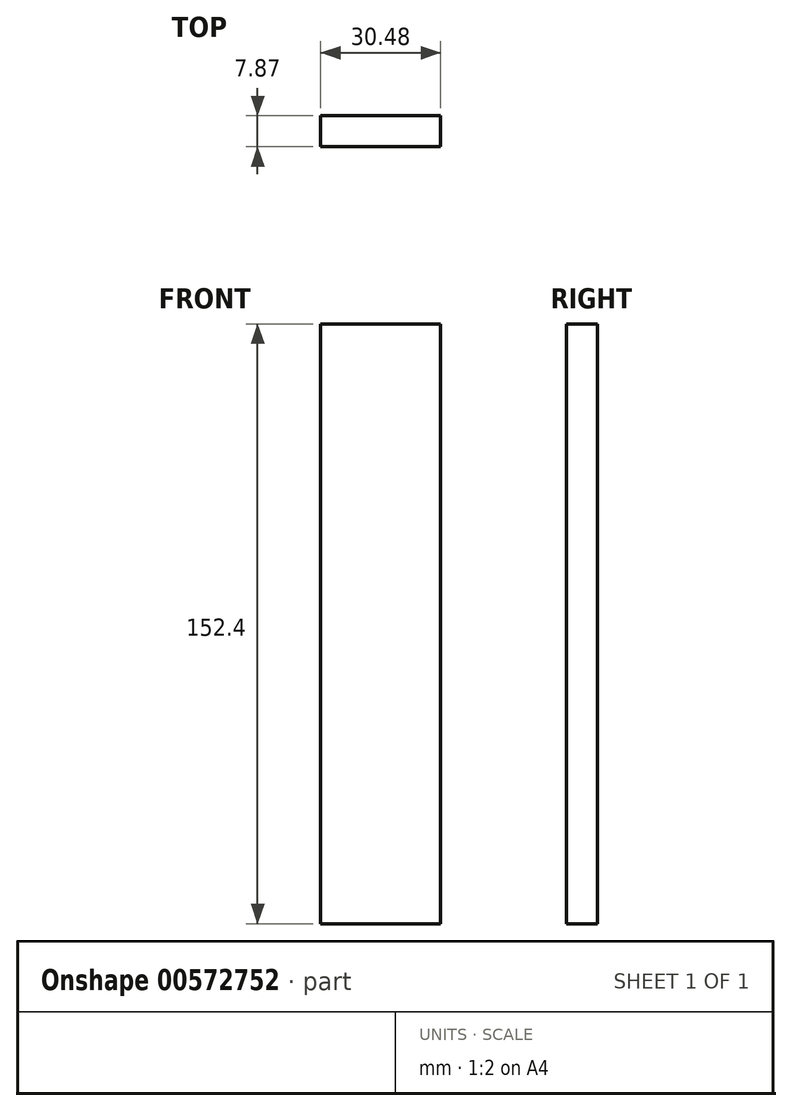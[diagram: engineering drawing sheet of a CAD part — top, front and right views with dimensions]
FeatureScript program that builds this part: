
annotation { "Feature Type Name" : "Feature", "Feature Type Description" : "" }
export const myFeature = defineFeature(function(context is Context, id is Id, definition is map)
    precondition{}
    {
        {
            var Q0;
            Q0=qCreatedBy(makeId("Front.planeOp"),FACE);
            var sketch = newSketch(context, id + "F0", { "sketchPlane" : qUnion([Q0])});
            skLineSegment(sketch, "E0.bottom", {"start": v(-6.64, 136.82) * mm, "end": v(23.84, 136.82) * mm});
            skLineSegment(sketch, "E0.top", {"start": v(-6.64, -15.58) * mm, "end": v(23.84, -15.58) * mm});
            skLineSegment(sketch, "E0.left", {"start": v(-6.64, 136.82) * mm, "end": v(-6.64, -15.58) * mm});
            skLineSegment(sketch, "E0.right", {"start": v(23.84, 136.82) * mm, "end": v(23.84, -15.58) * mm});
            skSolve(sketch);
        }
        {
            var Q0;
            Q0=makeQuery(id+"F0.imprint","IMPRINT",FACE,{"disambiguationData":[TD([[makeQuery(id+"F0.imprint","IMPRINT",EDGE,{"derivedFrom":sQuery(id+"F0.wireOp",EDGE,"E0.bottom")}),-1.0]])]});
            extrude(context, id + "F1", {"entities" : qUnion([Q0]), "depth" : 7.87 * mm, "offsetDistance" : 25.4 * mm});
        }
    });
